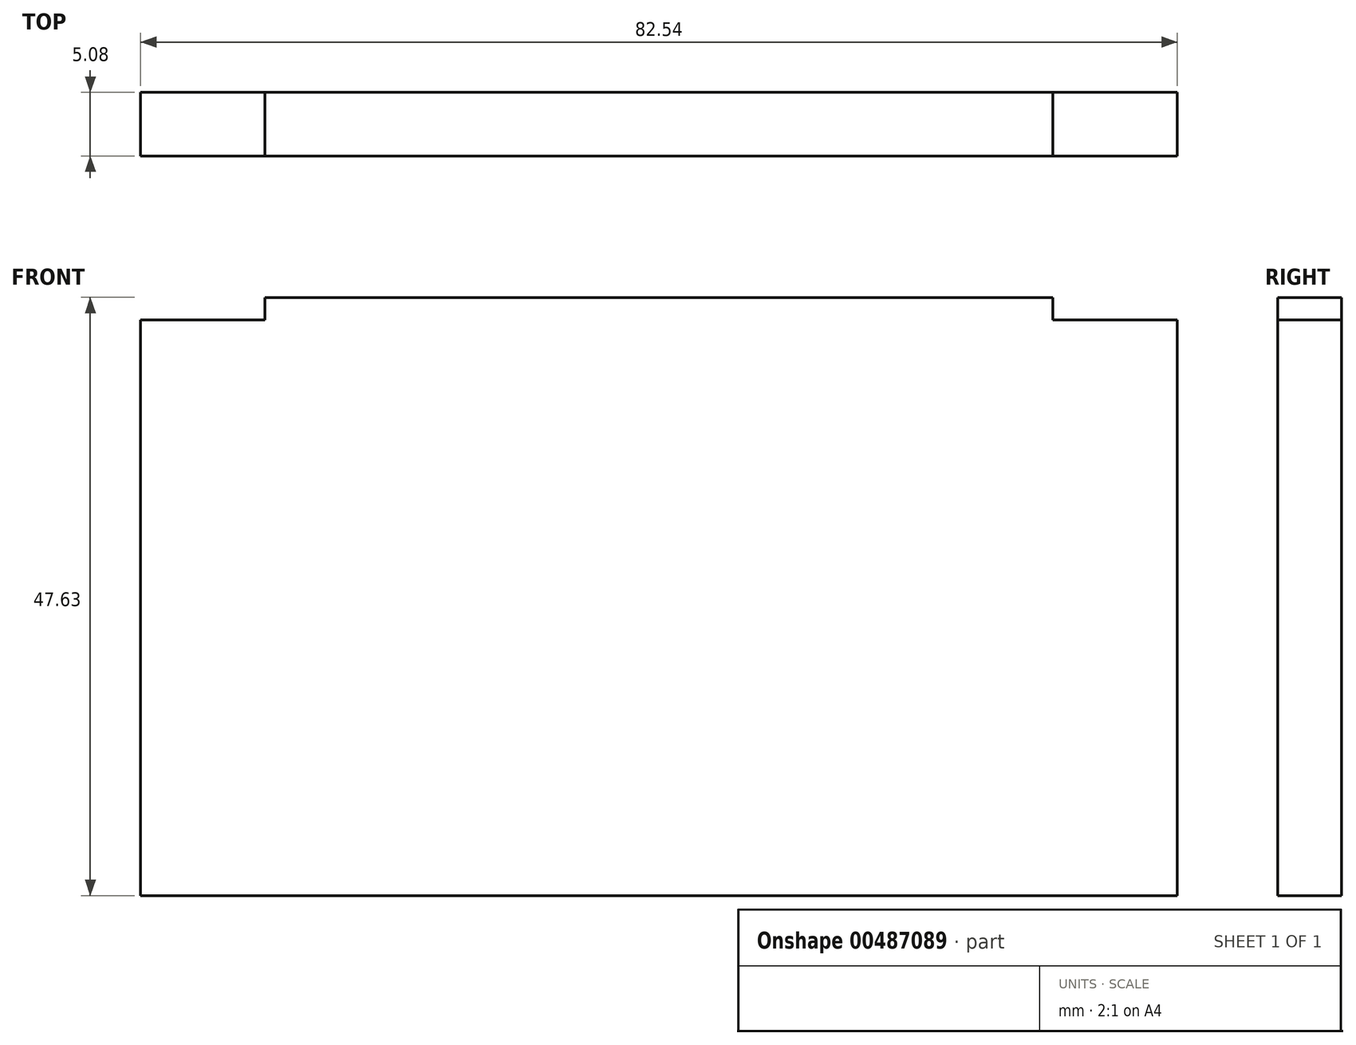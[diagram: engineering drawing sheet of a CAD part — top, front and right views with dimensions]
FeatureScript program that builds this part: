
annotation { "Feature Type Name" : "Feature", "Feature Type Description" : "" }
export const myFeature = defineFeature(function(context is Context, id is Id, definition is map)
    precondition{}
    {
        {
            var Q0;
            Q0=qCreatedBy(makeId("Front.planeOp"),FACE);
            var sketch = newSketch(context, id + "F0", { "sketchPlane" : qUnion([Q0])});
            skLineSegment(sketch, "E0.bottom", {"start": v(-31.37, 15.55) * mm, "end": v(31.37, 15.55) * mm});
            skLineSegment(sketch, "E0.top", {"start": v(-41.27, -32.08) * mm, "end": v(41.28, -32.08) * mm});
            skLineSegment(sketch, "E0.left", {"start": v(-41.28, 13.77) * mm, "end": v(-41.27, -32.08) * mm});
            skLineSegment(sketch, "E0.right", {"start": v(41.27, 13.77) * mm, "end": v(41.28, -32.08) * mm});
            skLineSegment(sketch, "E1.top", {"start": v(41.27, 13.77) * mm, "end": v(31.37, 13.77) * mm});
            skLineSegment(sketch, "E1.right", {"start": v(31.37, 15.55) * mm, "end": v(31.37, 13.77) * mm});
            skLineSegment(sketch, "E2.top", {"start": v(-41.27, 13.77) * mm, "end": v(-31.37, 13.77) * mm});
            skLineSegment(sketch, "E2.right", {"start": v(-31.37, 15.55) * mm, "end": v(-31.37, 13.77) * mm});
            skSolve(sketch);
        }
        {
            var Q0;
            Q0 = qSketchRegion(id + "F0", true);
            extrude(context, id + "F1", {"entities" : qUnion([Q0]), "depth" : 5.08 * mm});
        }
    });
